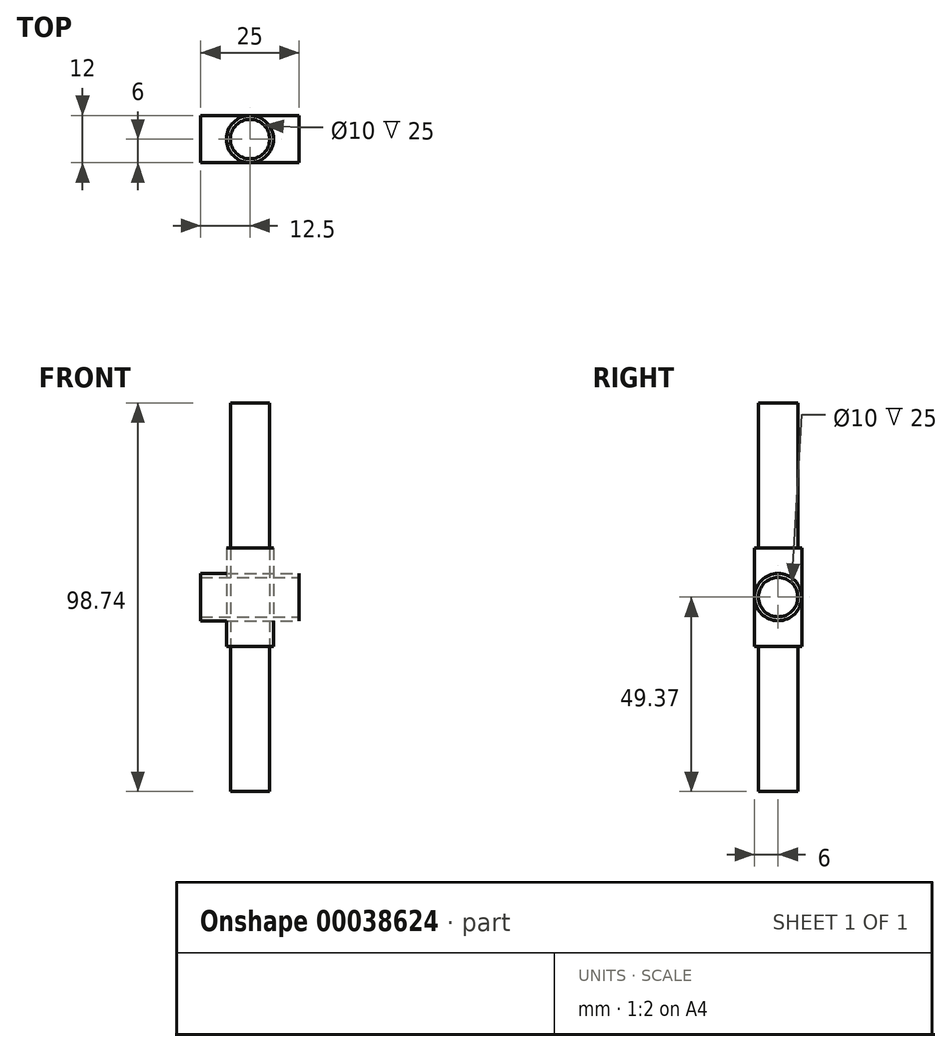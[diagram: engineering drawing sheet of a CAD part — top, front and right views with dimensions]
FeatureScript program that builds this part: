
annotation { "Feature Type Name" : "Feature", "Feature Type Description" : "" }
export const myFeature = defineFeature(function(context is Context, id is Id, definition is map)
    precondition{}
    {
        {
            var Q0;
            Q0=qCreatedBy(makeId("Top.planeOp"),FACE);
            var sketch = newSketch(context, id + "F0", { "sketchPlane" : qUnion([Q0])});
            skCircle(sketch, "E0", {"center": v(0, 0) * mm, "radius": 5 * mm});
            skCircle(sketch, "E1", {"center": v(0, 0) * mm, "radius": 6 * mm});
            skLineSegment(sketch, "E2", {"start": v(0, 0) * mm, "end": v(0, -6) * mm, "construction": true});
            skSolve(sketch);
        }
        {
            var Q0;
            Q0=makeQuery(id+"F0.imprint","IMPRINT",FACE,{"disambiguationData":[TD([[makeQuery(id+"F0.imprint","IMPRINT",EDGE,{"derivedFrom":sQuery(id+"F0.wireOp",EDGE,"E0")}),-1.0]])]});
            extrude(context, id + "F1", {"entities" : qUnion([Q0]), "endBound" : BoundingType.SYMMETRIC, "depth" : 25 * mm});
        }
        {
            var Q0;
            Q0=makeQuery(id+"F0.imprint","IMPRINT",FACE,{"disambiguationData":[TD([[makeQuery(id+"F0.imprint","IMPRINT",EDGE,{"derivedFrom":sQuery(id+"F0.wireOp",EDGE,"E0")}),1.0]])]});
            extrude(context, id + "F2", {"entities" : qUnion([Q0]), "endBound" : BoundingType.SYMMETRIC, "depth" : 98.73 * mm});
        }
        {
            var Q0;
            Q0=makeQuery(id+"F1.opExtrude","SWEPT_BODY",BODY,{"disambiguationData":[OSD([sQuery(id+"F0.wireOp",EDGE,"E0"),sQuery(id+"F0.wireOp",EDGE,"E1")])]});
            var Q1;
            Q1=sQuery(id+"F0.wireOp",EDGE,"E2");
            transform(context, id + "F3", {"entities" : qUnion([Q0]), "transformType" : TransformType.ROTATION, "transformAxis" : qUnion([Q1]), "angle" : 90 * degree, "makeCopy" : true});
        }
    });
